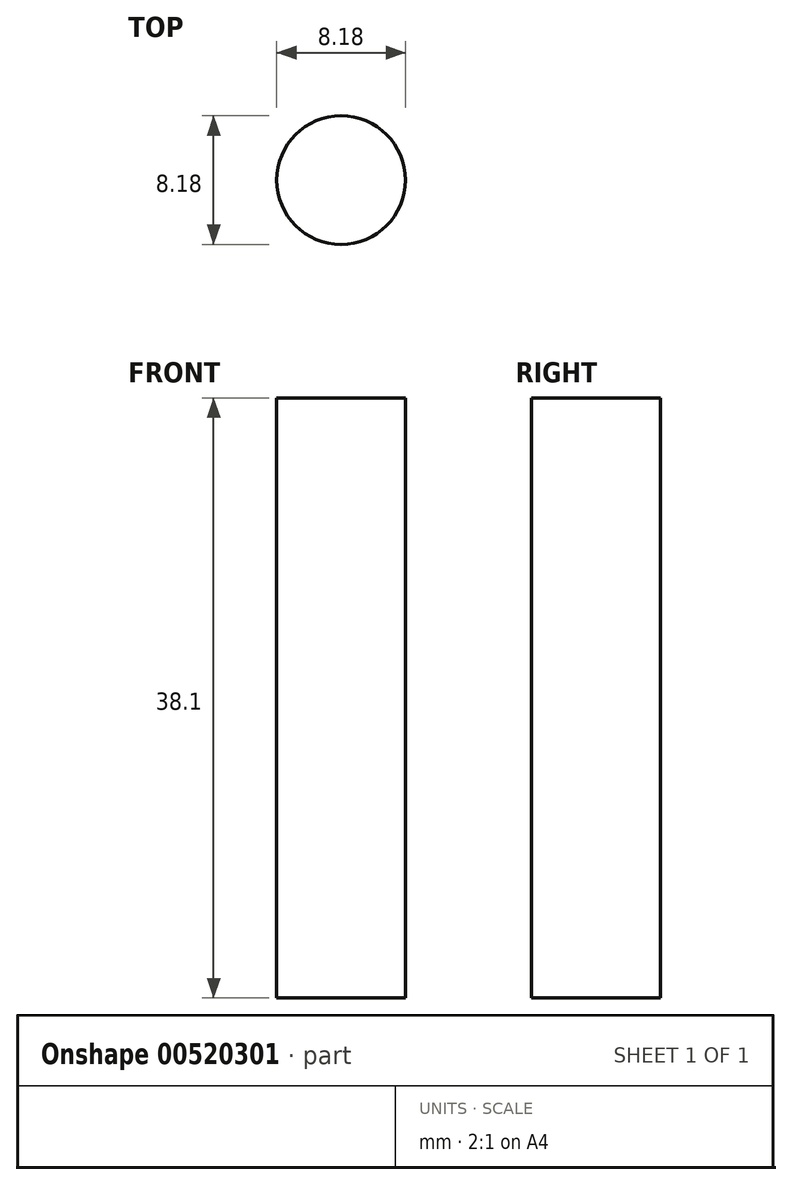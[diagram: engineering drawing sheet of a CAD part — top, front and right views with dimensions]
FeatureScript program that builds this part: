
annotation { "Feature Type Name" : "Feature", "Feature Type Description" : "" }
export const myFeature = defineFeature(function(context is Context, id is Id, definition is map)
    precondition{}
    {
        {
            var Q0;
            Q0=qCreatedBy(makeId("Top.planeOp"),FACE);
            var sketch = newSketch(context, id + "F0", { "sketchPlane" : qUnion([Q0])});
            skCircle(sketch, "E0", {"center": v(0, 0) * mm, "radius": 4.1 * mm});
            skSolve(sketch);
        }
        {
            var Q0;
            Q0 = qSketchRegion(id + "F0", true);
            extrude(context, id + "F1", {"entities" : qUnion([Q0]), "depth" : 38.1 * mm, "offsetDistance" : 25.4 * mm});
        }
    });
